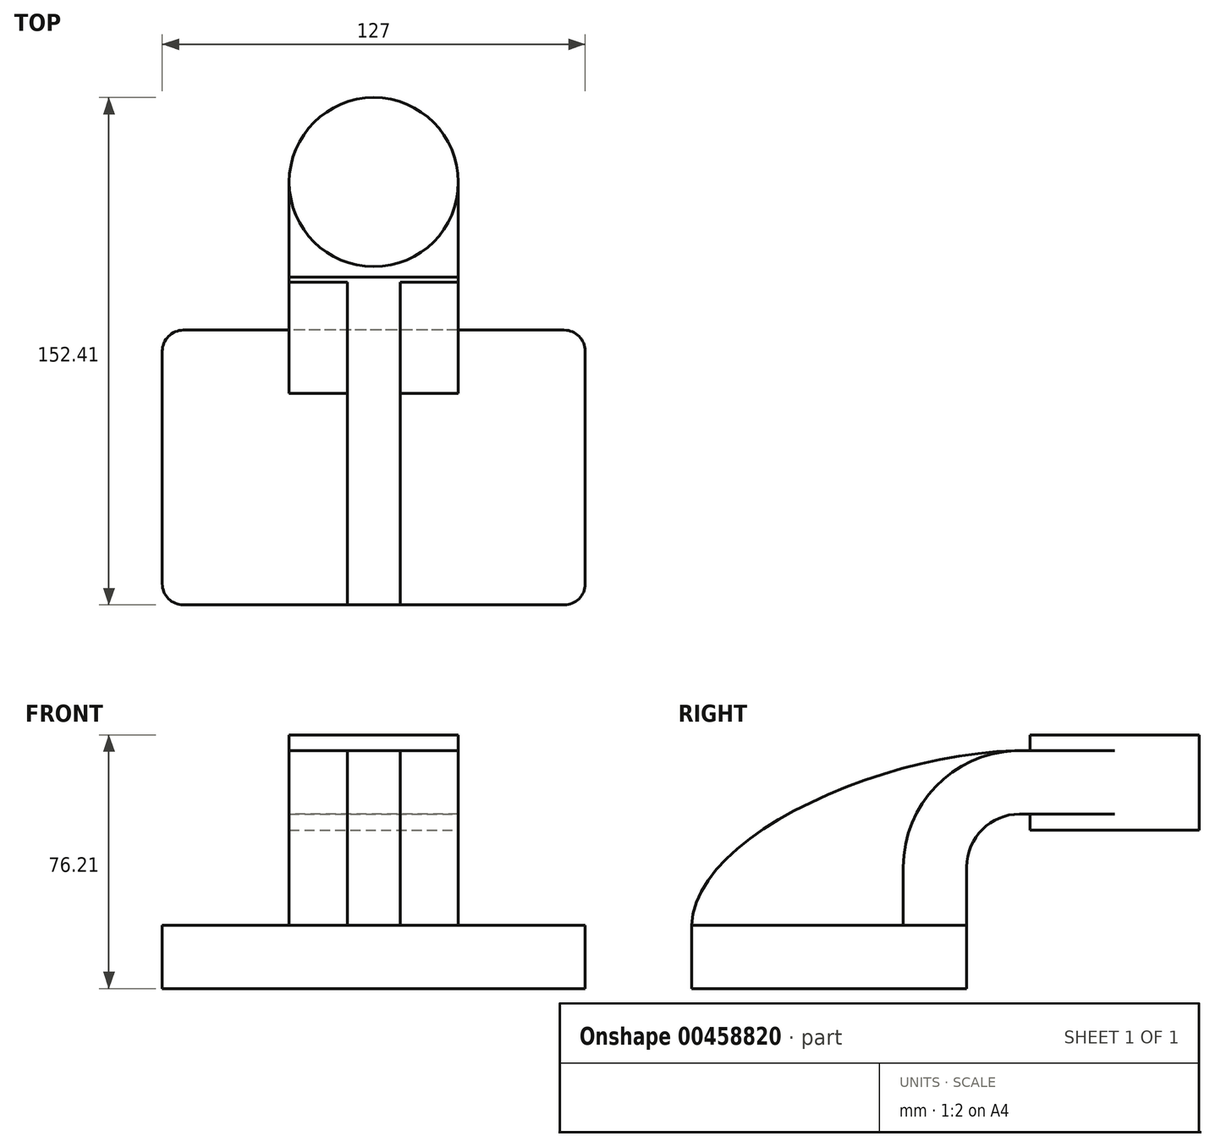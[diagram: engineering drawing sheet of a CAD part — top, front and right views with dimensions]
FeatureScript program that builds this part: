
annotation { "Feature Type Name" : "Feature", "Feature Type Description" : "" }
export const myFeature = defineFeature(function(context is Context, id is Id, definition is map)
    precondition{}
    {
        {
            var Q0;
            Q0=qCreatedBy(makeId("Right.planeOp"),FACE);
            var sketch = newSketch(context, id + "F0", { "sketchPlane" : qUnion([Q0])});
            skLineSegment(sketch, "E0.bottom", {"start": v(-41.28, -9.53) * mm, "end": v(41.28, -9.53) * mm});
            skLineSegment(sketch, "E0.top", {"start": v(-41.28, 9.53) * mm, "end": v(41.28, 9.53) * mm});
            skLineSegment(sketch, "E0.left", {"start": v(-41.28, -9.53) * mm, "end": v(-41.28, 9.53) * mm});
            skLineSegment(sketch, "E0.right", {"start": v(41.28, -9.53) * mm, "end": v(41.28, 9.52) * mm});
            skPoint(sketch, "E0.middle", {"position": v(0, 0) * mm});
            skLineSegment(sketch, "E1.bottom", {"start": v(111.12, 38.1) * mm, "end": v(60.32, 38.1) * mm});
            skLineSegment(sketch, "E1.top", {"start": v(111.12, 66.68) * mm, "end": v(60.32, 66.68) * mm});
            skLineSegment(sketch, "E1.left", {"start": v(111.12, 38.1) * mm, "end": v(111.12, 66.68) * mm});
            skLineSegment(sketch, "E1.right", {"start": v(60.32, 38.1) * mm, "end": v(60.32, 66.68) * mm});
            skPoint(sketch, "E1.middle", {"position": v(85.72, 52.39) * mm});
            skLineSegment(sketch, "E2", {"start": v(41.28, 9.52) * mm, "end": v(41.28, 27) * mm});
            skArc(sketch, "E3", {"start": v(41.27, 27) * mm, "mid": v(45.92, 38.23) * mm, "end": v(57.15, 42.88) * mm});
            skLineSegment(sketch, "E4", {"start": v(57.15, 42.88) * mm, "end": v(85.72, 42.88) * mm});
            skLineSegment(sketch, "E5.0", {"start": v(57.15, 61.93) * mm, "end": v(85.72, 61.93) * mm});
            skArc(sketch, "E5.1", {"start": v(22.22, 27) * mm, "mid": v(32.45, 51.7) * mm, "end": v(57.15, 61.93) * mm});
            skLineSegment(sketch, "E5.2", {"start": v(22.22, 9.52) * mm, "end": v(22.22, 27) * mm});
            skLineSegment(sketch, "E6", {"start": v(85.72, 38.1) * mm, "end": v(85.72, 66.68) * mm});
            skFitSpline(sketch, "E7", {"points": [v(-41.28, 9.53) * mm, v(57.15, 61.93) * mm], "startDerivative": vector(1.31, 79.67) * mm, "endDerivative": vector(124, 1.76) * mm});
            skSolve(sketch);
        }
        {
            var Q0;
            Q0=makeQuery(id+"F0.imprint","IMPRINT",FACE,{"disambiguationData":[TD([[makeQuery(id+"F0.imprint","IMPRINT",EDGE,{"derivedFrom":sQuery(id+"F0.wireOp",EDGE,"E0.bottom")}),1.0]])]});
            extrude(context, id + "F1", {"entities" : qUnion([Q0]), "depth" : 127 * mm, "symmetric" : true});
        }
        {
            var Q0;
            {var subQ1=sQuery(id+"F0.wireOp",EDGE,"E2");Q0=makeQuery(id+"F0.imprint","IMPRINT",FACE,{"disambiguationData":[TD([[makeQuery(id+"F0.imprint","IMPRINT",EDGE,{"derivedFrom":subQ1}),1.0]])]});}
            var Q1;
            {var subQ0=sQuery(id+"F0.wireOp",EDGE,"E4");var subQ1=sQuery(id+"F0.wireOp",EDGE,"E1.right");var subQ2=makeQuery(id+"F0.imprint","INTERSECT",VERTEX,{"derivedFrom":[subQ1,subQ0]});Q1=makeQuery(id+"F0.imprint","IMPRINT",FACE,{"disambiguationData":[TD([[makeQuery(id+"F0.imprint","IMPRINT",EDGE,{"disambiguationData":[TD([[subQ2,-1.0]])],"derivedFrom":subQ1}),-1.0]])]});}
            extrude(context, id + "F2", {"entities" : qUnion([Q0, Q1]), "operationType" : NewBodyOperationType.ADD, "depth" : 50.8 * mm, "symmetric" : true});
        }
        {
            var Q0;
            {var subQ3=sQuery(id+"F0.wireOp",EDGE,"E5.2");Q0=makeQuery(id+"F0.imprint","IMPRINT",FACE,{"disambiguationData":[TD([[makeQuery(id+"F0.imprint","IMPRINT",EDGE,{"derivedFrom":subQ3}),1.0]])]});}
            extrude(context, id + "F3", {"entities" : qUnion([Q0]), "operationType" : NewBodyOperationType.ADD, "depth" : 15.88 * mm, "symmetric" : true});
        }
        {
            var Q0;
            {var subQ0=sQuery(id+"F0.wireOp",EDGE,"E1.left");Q0=makeQuery(id+"F0.imprint","IMPRINT",FACE,{"disambiguationData":[TD([[makeQuery(id+"F0.imprint","IMPRINT",EDGE,{"derivedFrom":subQ0}),1.0]])]});}
            var Q1;
            Q1=sQuery(id+"F0.wireOp",EDGE,"E6");
            var Q2;
            Q2=sQuery(id+"F0.wireOp",EDGE,"E6");
            revolve(context, id + "F4", {"operationType" : NewBodyOperationType.ADD, "entities" : qUnion([Q0]), "surfaceEntities" : qUnion([Q1]), "axis" : qUnion([Q2]), "revolveType" : RevolveType.FULL});
        }
        {
            var Q0;
            Q0=makeQuery(id+"F1.opExtrude","CAP_EDGE",EDGE,{"disambiguationData":[OSD([sQuery(id+"F0.wireOp",EDGE,"E0.right")])],"isStart":false});
            var Q1;
            Q1=makeQuery(id+"F1.opExtrude","CAP_EDGE",EDGE,{"disambiguationData":[OSD([sQuery(id+"F0.wireOp",EDGE,"E0.left")])],"isStart":false});
            var Q2;
            Q2=makeQuery(id+"F1.opExtrude","CAP_EDGE",EDGE,{"disambiguationData":[OSD([sQuery(id+"F0.wireOp",EDGE,"E0.right")])],"isStart":true});
            var Q3;
            Q3=makeQuery(id+"F1.opExtrude","CAP_EDGE",EDGE,{"disambiguationData":[OSD([sQuery(id+"F0.wireOp",EDGE,"E0.left")])],"isStart":true});
            fillet(context, id + "F5", {"entities" : qUnion([Q0, Q1, Q2, Q3]), "radius" : 6.35 * mm, "tangentPropagation" : true, "allowEdgeOverflow" : false});
        }
    });
